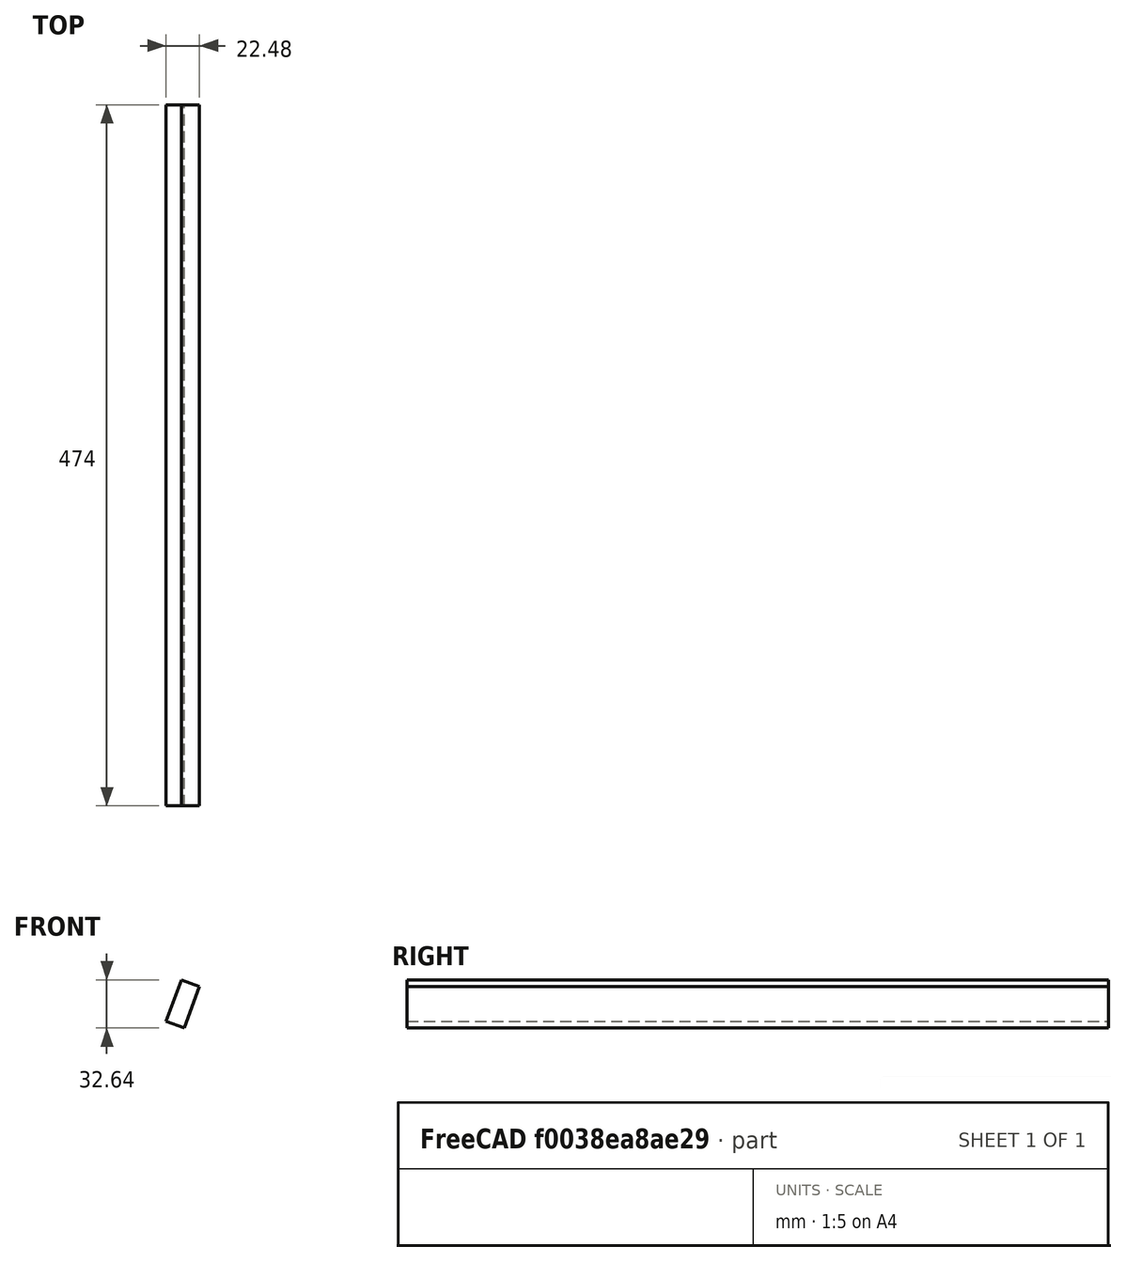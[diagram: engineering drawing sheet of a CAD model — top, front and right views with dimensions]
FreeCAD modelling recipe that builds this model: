
FCSTD DOCUMENT  (FreeCAD 0.19R24276 (Git))
Label: 4000_Body_front_YZ
License: All rights reserved
LicenseURL: http://en.wikipedia.org/wiki/All_rights_reserved
objects: Spreadsheet::Sheet×1, Sketcher::SketchObject×1, PartDesign::Pad×1, PartDesign::Body×1
note: 4 computed .brp shape members not serialized (recipe doc carries the construction recipe); baked Part::Feature solids carry a one-line shape summary decoded from their .brp

FEATURE [Spreadsheet::Sheet] Spreadsheet  label="xls"
  cells = B5=BODY FRONT; E5=nominal size; B6=Board Thickness; C6(thickness)=13; D6=xls.thickness; B7=Horizontal Y; C7(width)==+E7 - 2 * C6; D7=xls.width; E7=500; B8=X=; C8(height)=30; D8=xls.height; B9=Angle Y; C9(tilt)=70; D9=xls.tilt
FEATURE [Sketcher::SketchObject] Sketch
  FullyConstrained = false
  MapMode = 5
  Placement = pos=(0,0,0) rot=(1,0,0;1.5708rad)
  Support = -> [XZ_Plane]
  expr: Constraints[6] = <<xls>>.thickness
  expr: Constraints[7] = <<xls>>.height
  expr: Constraints[8] = <<xls>>.tilt
  sketch-geometry (4):
    g0: LineSegment StartX=12.216 StartY=-4.44626 StartZ=0 EndX=22.4766 EndY=23.7445 EndZ=0
    g1: LineSegment StartX=22.4766 StartY=23.7445 StartZ=0 EndX=10.2606 EndY=28.1908 EndZ=0
    g2: LineSegment StartX=10.2606 StartY=28.1908 StartZ=0 EndX=0 EndY=0 EndZ=0
    g3: LineSegment StartX=0 StartY=0 StartZ=0 EndX=12.216 EndY=-4.44626 EndZ=0
  constraints (11):
    c: Coincident(g0,g1)
    c: Coincident(g1,g2)
    c: Coincident(g2,g3)
    c: Parallel(g3,g1)
    c: Parallel(g0,g2)
    c: Perpendicular(g0,g3)
    c: Distance(g3) = 13
    c: Distance(g0) = 30
    c: Angle(g-1,g0) = 1.22173
    c: Coincident(g0,g3)
    c: Coincident(g-1,g2)
FEATURE [PartDesign::Pad] Pad
  AllowMultiFace = false
  Direction = (1,1,1)
  Length = 474
  Length2 = 100
  Placement = pos=(0,0,0) rot=(1,0,0;1.5708rad)
  Profile = -> Sketch
  Reversed = true
  Type = 0
  expr: Length = <<xls>>.width
FEATURE [PartDesign::Body] Body
  Group = -> [Sketch,Pad]
  Origin = -> Origin
  Tip = -> Pad
